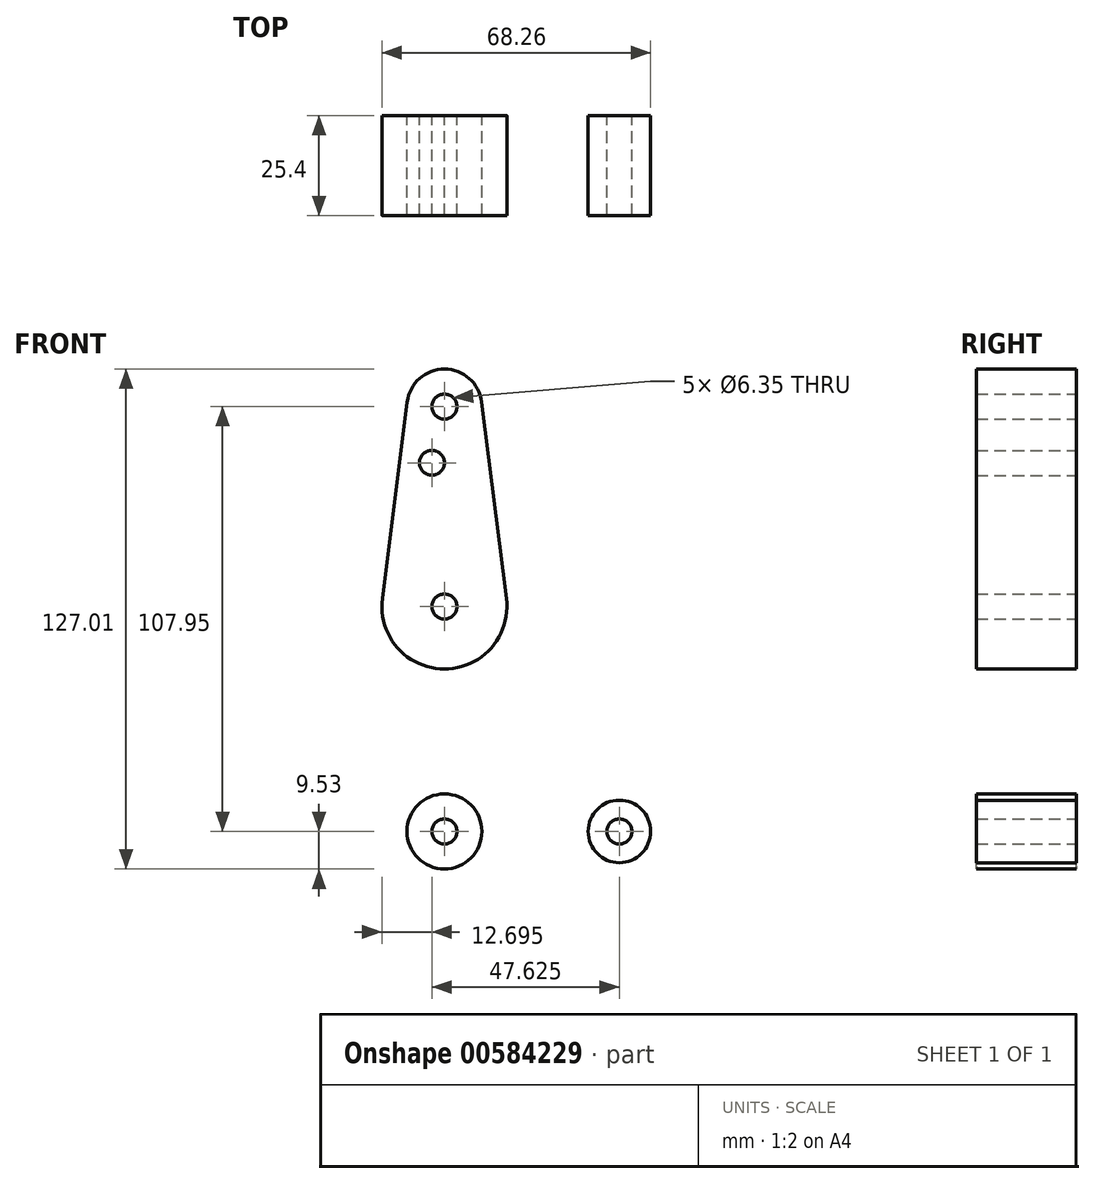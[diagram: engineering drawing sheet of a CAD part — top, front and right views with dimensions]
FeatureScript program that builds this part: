
annotation { "Feature Type Name" : "Feature", "Feature Type Description" : "" }
export const myFeature = defineFeature(function(context is Context, id is Id, definition is map)
    precondition{}
    {
        {
            var Q0;
            Q0=qCreatedBy(makeId("Front.planeOp"),FACE);
            var sketch = newSketch(context, id + "F0", { "sketchPlane" : qUnion([Q0])});
            skLineSegment(sketch, "E0", {"start": v(0, 0) * mm, "end": v(44.45, 0) * mm, "construction": true});
            skLineSegment(sketch, "E1", {"start": v(0, 0) * mm, "end": v(0, 57.15) * mm, "construction": true});
            skLineSegment(sketch, "E2", {"start": v(0, 57.15) * mm, "end": v(0, 107.95) * mm, "construction": true});
            skCircle(sketch, "E3", {"center": v(0, 107.95) * mm, "radius": 9.53 * mm});
            skCircle(sketch, "E4", {"center": v(0, 57.15) * mm, "radius": 15.88 * mm});
            skCircle(sketch, "E5", {"center": v(0, 0) * mm, "radius": 9.53 * mm});
            skCircle(sketch, "E6", {"center": v(44.45, 0) * mm, "radius": 7.94 * mm});
            skLineSegment(sketch, "E7", {"start": v(-15.75, 59.13) * mm, "end": v(-9.58, 0) * mm});
            skLineSegment(sketch, "E8", {"start": v(15.75, 59.13) * mm, "end": v(11.38, 17.63) * mm});
            skLineSegment(sketch, "E9", {"start": v(19, 8.85) * mm, "end": v(44.73, 7.93) * mm});
            skLineSegment(sketch, "E10", {"start": v(0, -9.53) * mm, "end": v(44.73, -7.93) * mm});
            skLineSegment(sketch, "E11", {"start": v(9.45, 109.14) * mm, "end": v(15.75, 59.13) * mm});
            skLineSegment(sketch, "E12", {"start": v(-9.45, 109.14) * mm, "end": v(-15.75, 59.13) * mm});
            skCircle(sketch, "E13", {"center": v(0, 57.15) * mm, "radius": 3.18 * mm});
            skCircle(sketch, "E14", {"center": v(0, 107.95) * mm, "radius": 3.18 * mm});
            skCircle(sketch, "E15", {"center": v(-3.18, 93.68) * mm, "radius": 3.18 * mm});
            skCircle(sketch, "E16", {"center": v(0, 0) * mm, "radius": 3.18 * mm});
            skCircle(sketch, "E17", {"center": v(44.45, 0) * mm, "radius": 3.18 * mm});
            skArc(sketch, "E18.filletArc", {"start": v(11.38, 17.63) * mm, "mid": v(13.28, 11.58) * mm, "end": v(19, 8.85) * mm});
            skSolve(sketch);
        }
        {
            var Q0;
            Q0 = qSketchRegion(id + "F0", true);
            extrude(context, id + "F1", {"entities" : qUnion([Q0]), "depth" : 25.4 * mm, "offsetDistance" : 25.4 * mm});
        }
    });
